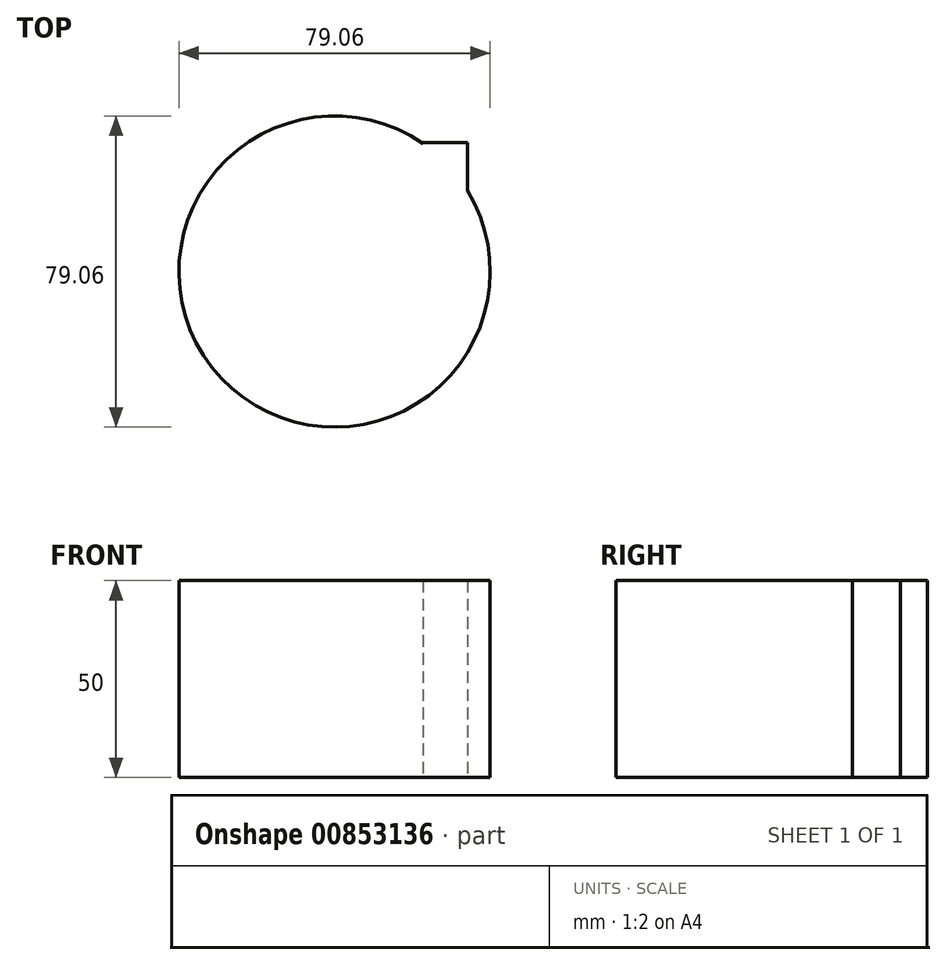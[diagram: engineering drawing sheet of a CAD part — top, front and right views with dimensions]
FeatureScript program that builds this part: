
annotation { "Feature Type Name" : "Feature", "Feature Type Description" : "" }
export const myFeature = defineFeature(function(context is Context, id is Id, definition is map)
    precondition{}
    {
        {
            var Q0;
            Q0=qCreatedBy(makeId("Top.planeOp"),FACE);
            var sketch = newSketch(context, id + "F0", { "sketchPlane" : qUnion([Q0])});
            skCircle(sketch, "E0", {"center": v(0, 0) * mm, "radius": 39.53 * mm});
            skSolve(sketch);
        }
        {
            var Q0;
            Q0=makeQuery(id+"F0.imprint","IMPRINT",FACE,{"disambiguationData":[TD([[makeQuery(id+"F0.imprint","IMPRINT",EDGE,{"derivedFrom":sQuery(id+"F0.wireOp",EDGE,"E0")}),1.0]])]});
            extrude(context, id + "F1", {"entities" : qUnion([Q0]), "depth" : 50 * mm, "offsetDistance" : 25 * mm});
        }
        {
            var Q0;
            Q0=qCreatedBy(makeId("Top.planeOp"),FACE);
            var sketch = newSketch(context, id + "F2", { "sketchPlane" : qUnion([Q0])});
            skLineSegment(sketch, "E1.bottom", {"start": v(33.78, 32.75) * mm, "end": v(22.46, 32.75) * mm});
            skLineSegment(sketch, "E1.top", {"start": v(33.78, 20.4) * mm, "end": v(22.46, 20.4) * mm});
            skLineSegment(sketch, "E1.left", {"start": v(33.78, 32.75) * mm, "end": v(33.78, 20.4) * mm});
            skLineSegment(sketch, "E1.right", {"start": v(22.46, 32.75) * mm, "end": v(22.46, 20.4) * mm});
            skSolve(sketch);
        }
        {
            var Q0;
            Q0 = qSketchRegion(id + "F2", true);
            extrude(context, id + "F3", {"entities" : qUnion([Q0]), "operationType" : NewBodyOperationType.ADD, "depth" : 50 * mm, "offsetDistance" : 25 * mm});
        }
    });
